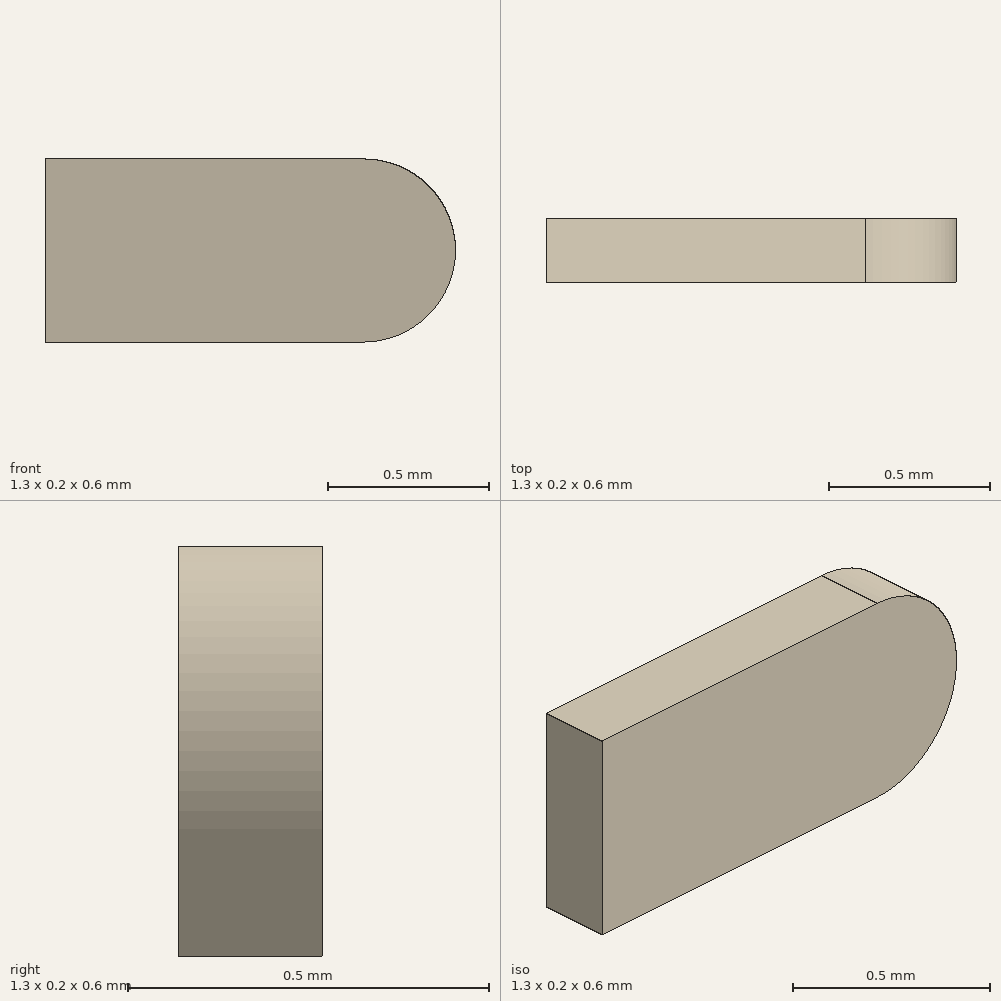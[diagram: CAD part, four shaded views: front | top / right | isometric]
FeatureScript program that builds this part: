
annotation { "Feature Type Name" : "Feature", "Feature Type Description" : "" }
export const myFeature = defineFeature(function(context is Context, id is Id, definition is map)
    precondition{}
    {
        {
            var Q0;
            Q0=qCreatedBy(makeId("Front.planeOp"),FACE);
            var sketch = newSketch(context, id + "F0", { "sketchPlane" : qUnion([Q0])});
            skLineSegment(sketch, "E0.bottom", {"start": v(0.5, 0.28) * mm, "end": v(-0.5, 0.28) * mm});
            skLineSegment(sketch, "E0.top", {"start": v(0.5, -0.28) * mm, "end": v(-0.5, -0.28) * mm});
            skLineSegment(sketch, "E0.left", {"start": v(0.5, 0.28) * mm, "end": v(0.5, -0.28) * mm});
            skLineSegment(sketch, "E0.right", {"start": v(-0.5, 0.28) * mm, "end": v(-0.5, -0.28) * mm});
            skPoint(sketch, "E0.middle", {"position": v(0, 0) * mm});
            skArc(sketch, "E1", {"start": v(0.5, -0.28) * mm, "mid": v(0.78, 0) * mm, "end": v(0.5, 0.28) * mm});
            skSolve(sketch);
        }
        {
            var Q0;
            Q0 = qSketchRegion(id + "F0", true);
            extrude(context, id + "F1", {"entities" : qUnion([Q0]), "depth" : .2 * mm});
        }
    });
